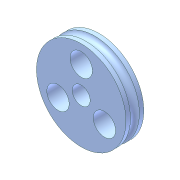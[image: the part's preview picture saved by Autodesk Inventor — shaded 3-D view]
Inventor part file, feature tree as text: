
AUTODESK INVENTOR PART (.ipt)
format: ipt  version: unknown  size: 206,848 bytes
history: native  units: mm
features: sketch x2, revolve x1, extrude x1, pattern_circular x1
ambient origin geometry x8: Origin, YZ Plane, XZ Plane, XY Plane, X Axis, Y Axis, Z Axis, Center Point
feature tree (5):
  revolve  "Revolution2"  [1 undecoded]
  extrude  "Extrusion2"  Depth=2.0mm
  pattern_circular  "Circular Pattern2"  Angle=90.0deg  [1 undecoded]
  sketch  "Sketch1"  dims[d0=2.0mm d14=10.0mm]
  sketch  "Sketch3"  dims[d15=2.0mm d16=2.0mm d17=90.0deg d18=6.0mm d19=5.0mm d20=10.0mm d21=0.0mm d22=30.0mm d23=360.0deg]
note: 2 required parameter values undecoded (feature->parameter linkage not recoverable at this tier; creation-order binding heuristic only, values carry confidence <= 0.55)